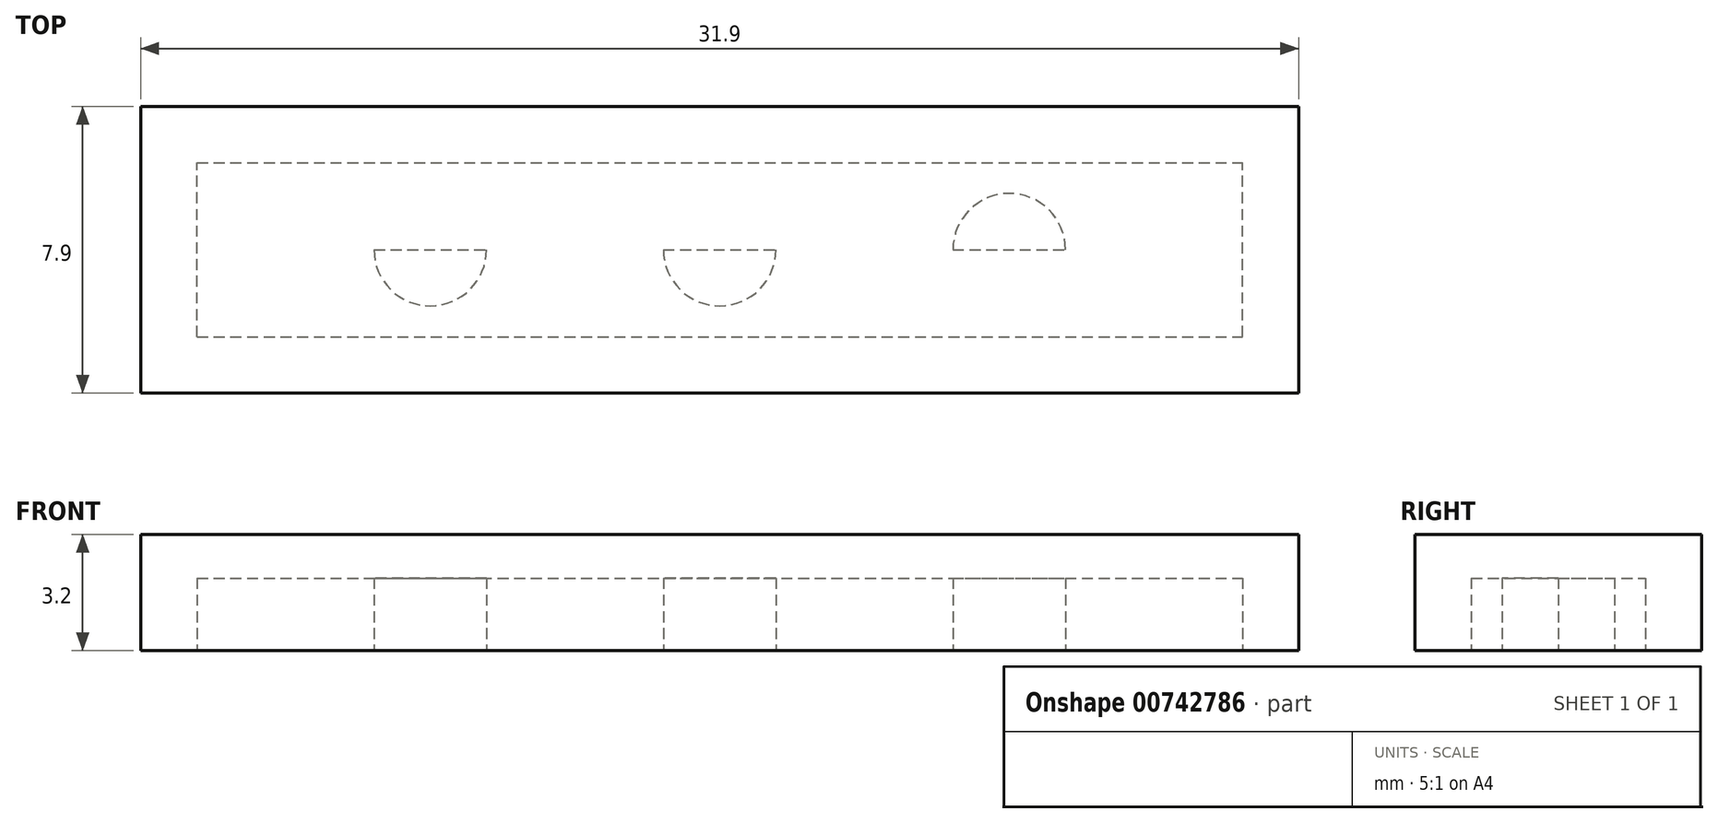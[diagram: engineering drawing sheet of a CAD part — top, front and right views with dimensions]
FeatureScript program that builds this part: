
annotation { "Feature Type Name" : "Feature", "Feature Type Description" : "" }
export const myFeature = defineFeature(function(context is Context, id is Id, definition is map)
    precondition{}
    {
        {
            var Q0;
            Q0=qCreatedBy(makeId("Top.planeOp"),FACE);
            var sketch = newSketch(context, id + "F0", { "sketchPlane" : qUnion([Q0])});
            skLineSegment(sketch, "E0.bottom", {"start": v(-11.1, 3.15) * mm, "end": v(20.8, 3.15) * mm});
            skLineSegment(sketch, "E0.top", {"start": v(-11.1, -4.75) * mm, "end": v(20.8, -4.75) * mm});
            skLineSegment(sketch, "E0.left", {"start": v(-11.1, 3.15) * mm, "end": v(-11.1, -4.75) * mm});
            skLineSegment(sketch, "E0.right", {"start": v(20.8, 3.15) * mm, "end": v(20.8, -4.75) * mm});
            skSolve(sketch);
        }
        {
            var Q0;
            Q0=makeQuery(id+"F0.imprint","IMPRINT",FACE,{"disambiguationData":[TD([[makeQuery(id+"F0.imprint","IMPRINT",EDGE,{"derivedFrom":sQuery(id+"F0.wireOp",EDGE,"E0.bottom")}),-1.0]])]});
            var Q1;
            Q1=makeQuery(id+"F0.imprint","IMPRINT",FACE,{"disambiguationData":[TD([[makeQuery(id+"F0.imprint","IMPRINT",EDGE,{"derivedFrom":sQuery(id+"F0.wireOp",EDGE,"E0.bottom")}),-1.0]])]});
            extrude(context, id + "F1", {"entities" : qUnion([Q0, Q1]), "depth" : 3.2 * mm, "offsetDistance" : 25 * mm});
        }
        {
            var Q0;
            Q0=makeQuery(id+"F1.opExtrude","CAP_FACE",FACE,{"disambiguationData":[OSD([sQuery(id+"F0.wireOp",EDGE,"E0.bottom"),sQuery(id+"F0.wireOp",EDGE,"E0.top"),sQuery(id+"F0.wireOp",EDGE,"E0.left"),sQuery(id+"F0.wireOp",EDGE,"E0.right")])],"isStart":true});
            var sketch = newSketch(context, id + "F2", { "sketchPlane" : qUnion([Q0])});
            skLineSegment(sketch, "E1.bottom", {"start": v(-9.56, 3.2) * mm, "end": v(19.24, 3.2) * mm});
            skLineSegment(sketch, "E1.top", {"start": v(-9.56, -1.6) * mm, "end": v(19.24, -1.6) * mm});
            skLineSegment(sketch, "E1.left", {"start": v(-9.56, 3.2) * mm, "end": v(-9.56, -1.6) * mm});
            skLineSegment(sketch, "E1.right", {"start": v(19.24, 3.2) * mm, "end": v(19.24, -1.6) * mm});
            skLineSegment(sketch, "E2", {"start": v(4.84, 4.75) * mm, "end": v(4.84, -3.15) * mm});
            skLineSegment(sketch, "E3", {"start": v(-3.13, 4.75) * mm, "end": v(-3.13, -3.15) * mm});
            skLineSegment(sketch, "E4", {"start": v(12.82, -3.15) * mm, "end": v(12.82, 4.75) * mm});
            skLineSegment(sketch, "E5", {"start": v(-11.1, 0.8) * mm, "end": v(20.8, 0.8) * mm});
            skCircle(sketch, "E6", {"center": v(-3.13, 0.8) * mm, "radius": 1.55 * mm});
            skCircle(sketch, "E7", {"center": v(4.84, 0.8) * mm, "radius": 1.55 * mm});
            skCircle(sketch, "E8", {"center": v(12.82, 0.8) * mm, "radius": 1.55 * mm});
            skCircle(sketch, "E9", {"center": v(-3.13, 0.8) * mm, "radius": 0.75 * mm});
            skCircle(sketch, "E10", {"center": v(4.84, 0.8) * mm, "radius": 0.75 * mm});
            skCircle(sketch, "E11", {"center": v(12.82, 0.8) * mm, "radius": 0.75 * mm});
            skSolve(sketch);
        }
        {
            var Q0;
            {var subQ1=sQuery(id+"F2.wireOp",EDGE,"E1.left");var subQ6=sQuery(id+"F2.wireOp",EDGE,"E1.bottom");var subQ9=makeQuery(id+"F2.imprint","INTERSECT",VERTEX,{"derivedFrom":[subQ6,subQ1]});Q0=makeQuery(id+"F2.imprint","IMPRINT",FACE,{"disambiguationData":[TD([[makeQuery(id+"F2.imprint","IMPRINT",EDGE,{"disambiguationData":[TD([[subQ9,-1.0]])],"derivedFrom":subQ6}),-1.0]])]});}
            var Q1;
            {var subQ6=sQuery(id+"F2.wireOp",EDGE,"E1.bottom");var subQ9=sQuery(id+"F2.wireOp",EDGE,"E3");var subQ10=makeQuery(id+"F2.imprint","INTERSECT",VERTEX,{"derivedFrom":[subQ6,subQ9]});Q1=makeQuery(id+"F2.imprint","IMPRINT",FACE,{"disambiguationData":[TD([[makeQuery(id+"F2.imprint","IMPRINT",EDGE,{"disambiguationData":[TD([[subQ10,-1.0]])],"derivedFrom":subQ6}),-1.0]])]});}
            var Q2;
            {var subQ1=sQuery(id+"F2.wireOp",EDGE,"E1.bottom");var subQ5=sQuery(id+"F2.wireOp",EDGE,"E2");var subQ6=makeQuery(id+"F2.imprint","INTERSECT",VERTEX,{"derivedFrom":[subQ1,subQ5]});Q2=makeQuery(id+"F2.imprint","IMPRINT",FACE,{"disambiguationData":[TD([[makeQuery(id+"F2.imprint","IMPRINT",EDGE,{"disambiguationData":[TD([[subQ6,-1.0]])],"derivedFrom":subQ1}),-1.0]])]});}
            var Q3;
            {var subQ1=sQuery(id+"F2.wireOp",EDGE,"E1.right");var subQ6=sQuery(id+"F2.wireOp",EDGE,"E1.bottom");var subQ9=makeQuery(id+"F2.imprint","INTERSECT",VERTEX,{"derivedFrom":[subQ6,subQ1]});Q3=makeQuery(id+"F2.imprint","IMPRINT",FACE,{"disambiguationData":[TD([[makeQuery(id+"F2.imprint","IMPRINT",EDGE,{"disambiguationData":[TD([[subQ9,1.0]])],"derivedFrom":subQ6}),-1.0]])]});}
            var Q4;
            {var subQ1=sQuery(id+"F2.wireOp",EDGE,"E1.top");var subQ5=sQuery(id+"F2.wireOp",EDGE,"E1.right");var subQ6=makeQuery(id+"F2.imprint","INTERSECT",VERTEX,{"derivedFrom":[subQ1,subQ5]});Q4=makeQuery(id+"F2.imprint","IMPRINT",FACE,{"disambiguationData":[TD([[makeQuery(id+"F2.imprint","IMPRINT",EDGE,{"disambiguationData":[TD([[subQ6,1.0]])],"derivedFrom":subQ1}),1.0]])]});}
            var Q5;
            {var subQ6=sQuery(id+"F2.wireOp",EDGE,"E1.top");var subQ9=sQuery(id+"F2.wireOp",EDGE,"E2");var subQ10=makeQuery(id+"F2.imprint","INTERSECT",VERTEX,{"derivedFrom":[subQ6,subQ9]});Q5=makeQuery(id+"F2.imprint","IMPRINT",FACE,{"disambiguationData":[TD([[makeQuery(id+"F2.imprint","IMPRINT",EDGE,{"disambiguationData":[TD([[subQ10,-1.0]])],"derivedFrom":subQ6}),1.0]])]});}
            var Q6;
            {var subQ5=sQuery(id+"F2.wireOp",EDGE,"E3");var subQ6=sQuery(id+"F2.wireOp",EDGE,"E1.top");var subQ7=makeQuery(id+"F2.imprint","INTERSECT",VERTEX,{"derivedFrom":[subQ6,subQ5]});Q6=makeQuery(id+"F2.imprint","IMPRINT",FACE,{"disambiguationData":[TD([[makeQuery(id+"F2.imprint","IMPRINT",EDGE,{"disambiguationData":[TD([[subQ7,-1.0]])],"derivedFrom":subQ6}),1.0]])]});}
            var Q7;
            {var subQ1=sQuery(id+"F2.wireOp",EDGE,"E1.left");var subQ6=sQuery(id+"F2.wireOp",EDGE,"E1.top");var subQ9=makeQuery(id+"F2.imprint","INTERSECT",VERTEX,{"derivedFrom":[subQ6,subQ1]});Q7=makeQuery(id+"F2.imprint","IMPRINT",FACE,{"disambiguationData":[TD([[makeQuery(id+"F2.imprint","IMPRINT",EDGE,{"disambiguationData":[TD([[subQ9,-1.0]])],"derivedFrom":subQ6}),1.0]])]});}
            var Q8;
            {var subQ0=sQuery(id+"F2.wireOp",EDGE,"E9");var subQ1=sQuery(id+"F2.wireOp",EDGE,"E3");var subQ2=makeQuery(id+"F2.imprint","INTERSECT",VERTEX,{"disambiguationData":[OD(0.0)],"derivedFrom":[subQ1,subQ0]});Q8=makeQuery(id+"F2.imprint","IMPRINT",FACE,{"disambiguationData":[TD([[makeQuery(id+"F2.imprint","IMPRINT",EDGE,{"disambiguationData":[TD([[subQ2,-1.0]])],"derivedFrom":subQ1}),-1.0]])]});}
            var Q9;
            {var subQ0=sQuery(id+"F2.wireOp",EDGE,"E5");var subQ1=sQuery(id+"F2.wireOp",EDGE,"E3");var subQ2=makeQuery(id+"F2.imprint","INTERSECT",VERTEX,{"derivedFrom":[subQ1,subQ0]});Q9=makeQuery(id+"F2.imprint","IMPRINT",FACE,{"disambiguationData":[TD([[makeQuery(id+"F2.imprint","IMPRINT",EDGE,{"disambiguationData":[TD([[subQ2,-1.0]])],"derivedFrom":subQ1}),-1.0]])]});}
            var Q10;
            {var subQ0=sQuery(id+"F2.wireOp",EDGE,"E5");var subQ1=sQuery(id+"F2.wireOp",EDGE,"E3");var subQ2=makeQuery(id+"F2.imprint","INTERSECT",VERTEX,{"derivedFrom":[subQ1,subQ0]});Q10=makeQuery(id+"F2.imprint","IMPRINT",FACE,{"disambiguationData":[TD([[makeQuery(id+"F2.imprint","IMPRINT",EDGE,{"disambiguationData":[TD([[subQ2,-1.0]])],"derivedFrom":subQ1}),1.0]])]});}
            var Q11;
            {var subQ0=sQuery(id+"F2.wireOp",EDGE,"E9");var subQ1=sQuery(id+"F2.wireOp",EDGE,"E3");var subQ2=makeQuery(id+"F2.imprint","INTERSECT",VERTEX,{"disambiguationData":[OD(0.0)],"derivedFrom":[subQ1,subQ0]});Q11=makeQuery(id+"F2.imprint","IMPRINT",FACE,{"disambiguationData":[TD([[makeQuery(id+"F2.imprint","IMPRINT",EDGE,{"disambiguationData":[TD([[subQ2,-1.0]])],"derivedFrom":subQ1}),1.0]])]});}
            var Q12;
            {var subQ0=sQuery(id+"F2.wireOp",EDGE,"E10");var subQ1=sQuery(id+"F2.wireOp",EDGE,"E2");var subQ2=makeQuery(id+"F2.imprint","INTERSECT",VERTEX,{"disambiguationData":[OD(0.0)],"derivedFrom":[subQ1,subQ0]});Q12=makeQuery(id+"F2.imprint","IMPRINT",FACE,{"disambiguationData":[TD([[makeQuery(id+"F2.imprint","IMPRINT",EDGE,{"disambiguationData":[TD([[subQ2,-1.0]])],"derivedFrom":subQ1}),-1.0]])]});}
            var Q13;
            {var subQ0=sQuery(id+"F2.wireOp",EDGE,"E10");var subQ1=sQuery(id+"F2.wireOp",EDGE,"E2");var subQ2=makeQuery(id+"F2.imprint","INTERSECT",VERTEX,{"disambiguationData":[OD(0.0)],"derivedFrom":[subQ1,subQ0]});Q13=makeQuery(id+"F2.imprint","IMPRINT",FACE,{"disambiguationData":[TD([[makeQuery(id+"F2.imprint","IMPRINT",EDGE,{"disambiguationData":[TD([[subQ2,-1.0]])],"derivedFrom":subQ1}),1.0]])]});}
            var Q14;
            {var subQ0=sQuery(id+"F2.wireOp",EDGE,"E5");var subQ1=sQuery(id+"F2.wireOp",EDGE,"E2");var subQ2=makeQuery(id+"F2.imprint","INTERSECT",VERTEX,{"derivedFrom":[subQ1,subQ0]});Q14=makeQuery(id+"F2.imprint","IMPRINT",FACE,{"disambiguationData":[TD([[makeQuery(id+"F2.imprint","IMPRINT",EDGE,{"disambiguationData":[TD([[subQ2,-1.0]])],"derivedFrom":subQ1}),-1.0]])]});}
            var Q15;
            {var subQ0=sQuery(id+"F2.wireOp",EDGE,"E5");var subQ1=sQuery(id+"F2.wireOp",EDGE,"E2");var subQ2=makeQuery(id+"F2.imprint","INTERSECT",VERTEX,{"derivedFrom":[subQ1,subQ0]});Q15=makeQuery(id+"F2.imprint","IMPRINT",FACE,{"disambiguationData":[TD([[makeQuery(id+"F2.imprint","IMPRINT",EDGE,{"disambiguationData":[TD([[subQ2,-1.0]])],"derivedFrom":subQ1}),1.0]])]});}
            var Q16;
            {var subQ0=sQuery(id+"F2.wireOp",EDGE,"E5");var subQ1=sQuery(id+"F2.wireOp",EDGE,"E4");var subQ2=makeQuery(id+"F2.imprint","INTERSECT",VERTEX,{"derivedFrom":[subQ1,subQ0]});Q16=makeQuery(id+"F2.imprint","IMPRINT",FACE,{"disambiguationData":[TD([[makeQuery(id+"F2.imprint","IMPRINT",EDGE,{"disambiguationData":[TD([[subQ2,-1.0]])],"derivedFrom":subQ1}),1.0]])]});}
            var Q17;
            {var subQ0=sQuery(id+"F2.wireOp",EDGE,"E5");var subQ1=sQuery(id+"F2.wireOp",EDGE,"E4");var subQ2=makeQuery(id+"F2.imprint","INTERSECT",VERTEX,{"derivedFrom":[subQ1,subQ0]});Q17=makeQuery(id+"F2.imprint","IMPRINT",FACE,{"disambiguationData":[TD([[makeQuery(id+"F2.imprint","IMPRINT",EDGE,{"disambiguationData":[TD([[subQ2,-1.0]])],"derivedFrom":subQ1}),-1.0]])]});}
            var Q18;
            {var subQ0=sQuery(id+"F2.wireOp",EDGE,"E11");var subQ1=sQuery(id+"F2.wireOp",EDGE,"E4");var subQ2=makeQuery(id+"F2.imprint","INTERSECT",VERTEX,{"disambiguationData":[OD(0.0)],"derivedFrom":[subQ1,subQ0]});Q18=makeQuery(id+"F2.imprint","IMPRINT",FACE,{"disambiguationData":[TD([[makeQuery(id+"F2.imprint","IMPRINT",EDGE,{"disambiguationData":[TD([[subQ2,-1.0]])],"derivedFrom":subQ1}),-1.0]])]});}
            var Q19;
            {var subQ0=sQuery(id+"F2.wireOp",EDGE,"E11");var subQ1=sQuery(id+"F2.wireOp",EDGE,"E4");var subQ2=makeQuery(id+"F2.imprint","INTERSECT",VERTEX,{"disambiguationData":[OD(0.0)],"derivedFrom":[subQ1,subQ0]});Q19=makeQuery(id+"F2.imprint","IMPRINT",FACE,{"disambiguationData":[TD([[makeQuery(id+"F2.imprint","IMPRINT",EDGE,{"disambiguationData":[TD([[subQ2,-1.0]])],"derivedFrom":subQ1}),1.0]])]});}
            extrude(context, id + "F3", {"entities" : qUnion([Q0, Q1, Q2, Q3, Q4, Q5, Q6, Q7, Q8, Q9, Q10, Q11, Q12, Q13, Q14, Q15, Q16, Q17, Q18, Q19]), "operationType" : NewBodyOperationType.REMOVE, "oppositeDirection" : true, "depth" : 2 * mm, "offsetDistance" : 25 * mm});
        }
    });
